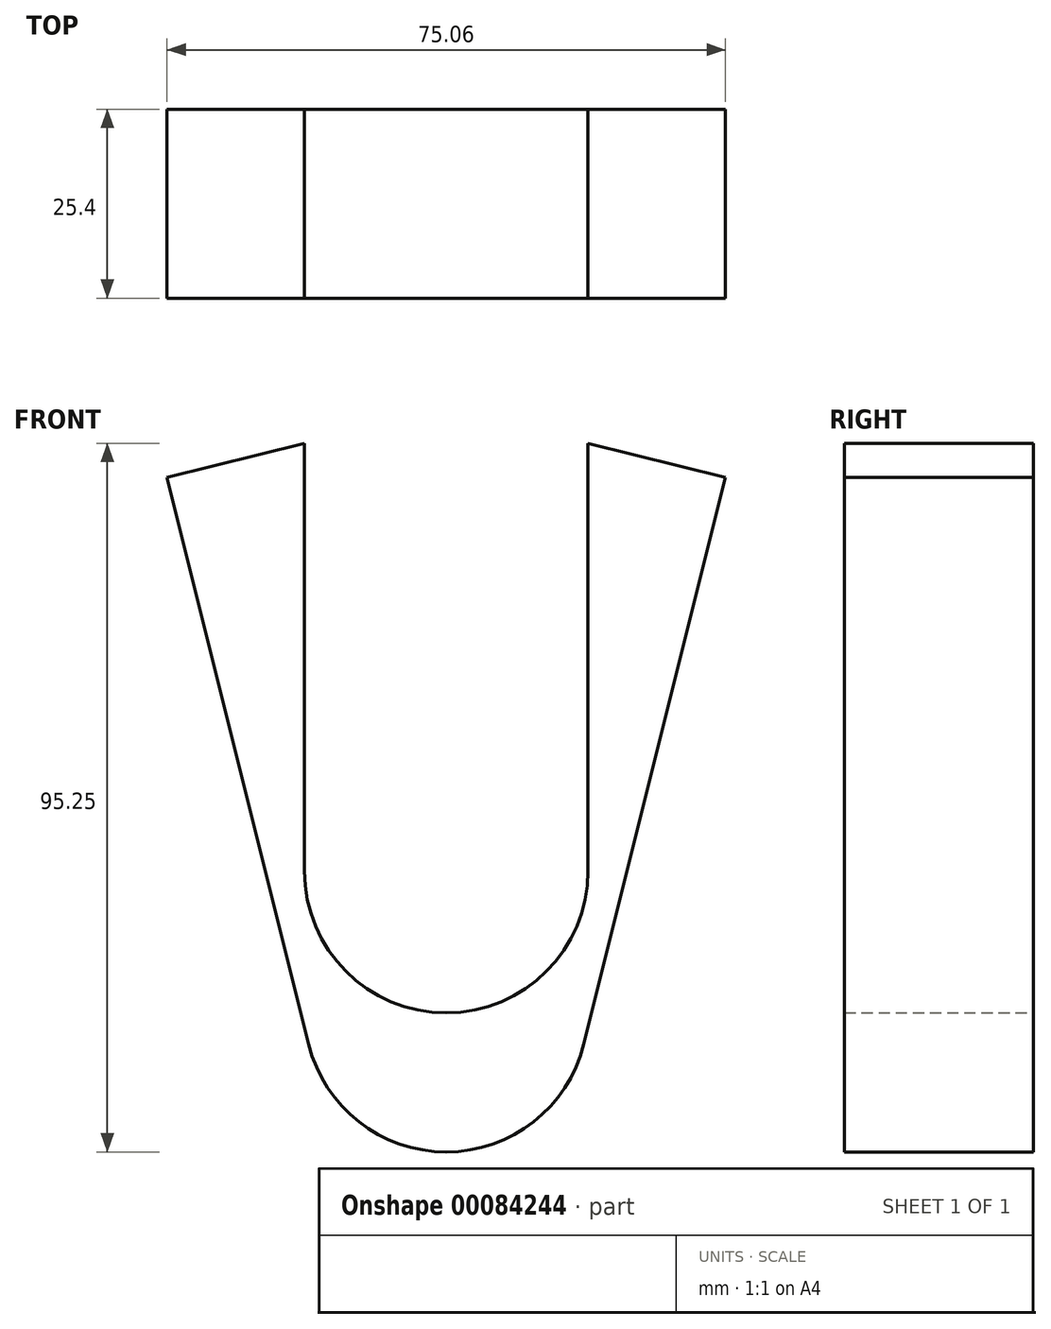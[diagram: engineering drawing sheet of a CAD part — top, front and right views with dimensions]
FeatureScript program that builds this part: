
annotation { "Feature Type Name" : "Feature", "Feature Type Description" : "" }
export const myFeature = defineFeature(function(context is Context, id is Id, definition is map)
    precondition{}
    {
        {
            var Q0;
            Q0=qCreatedBy(makeId("Front.planeOp"),FACE);
            var sketch = newSketch(context, id + "F0", { "sketchPlane" : qUnion([Q0])});
            skLineSegment(sketch, "E0", {"start": v(0, 0) * mm, "end": v(19.05, 0) * mm, "construction": true});
            skLineSegment(sketch, "E1", {"start": v(0, 0) * mm, "end": v(0, -76.2) * mm, "construction": true});
            skLineSegment(sketch, "E2", {"start": v(19.05, 0) * mm, "end": v(-19.05, 0) * mm, "construction": true});
            skLineSegment(sketch, "E3", {"start": v(19.05, 0) * mm, "end": v(0, -76.2) * mm});
            skLineSegment(sketch, "E4", {"start": v(-19.05, 0) * mm, "end": v(0, -76.2) * mm});
            skLineSegment(sketch, "E5", {"start": v(19.05, 0) * mm, "end": v(37.53, -4.62) * mm});
            skLineSegment(sketch, "E6", {"start": v(0, -76.2) * mm, "end": v(18.48, -80.82) * mm});
            skLineSegment(sketch, "E7", {"start": v(37.53, -4.62) * mm, "end": v(18.48, -80.82) * mm});
            skLineSegment(sketch, "E8.MirrorCS", {"start": v(-19.05, 0) * mm, "end": v(-37.53, -4.62) * mm});
            skLineSegment(sketch, "E9.MirrorCS", {"start": v(-37.53, -4.62) * mm, "end": v(-18.48, -80.82) * mm});
            skLineSegment(sketch, "E10.MirrorCS", {"start": v(0, -76.2) * mm, "end": v(-18.48, -80.82) * mm});
            skArc(sketch, "E11", {"start": v(-18.48, -80.82) * mm, "mid": v(0, -95.25) * mm, "end": v(18.48, -80.82) * mm});
            skSolve(sketch);
        }
        {
            var Q0;
            Q0 = qSketchRegion(id + "F0", true);
            extrude(context, id + "F1", {"entities" : qUnion([Q0]), "endBound" : BoundingType.SYMMETRIC, "depth" : 25.4 * mm});
        }
        {
            var Q0;
            Q0=qCreatedBy(makeId("Front.planeOp"),FACE);
            var sketch = newSketch(context, id + "F2", { "sketchPlane" : qUnion([Q0])});
            skLineSegment(sketch, "E12", {"start": v(0, 0) * mm, "end": v(19.05, 0) * mm, "construction": true});
            skLineSegment(sketch, "E13", {"start": v(0, 0) * mm, "end": v(0, -76.55) * mm, "construction": true});
            skLineSegment(sketch, "E14", {"start": v(-19.05, -57.5) * mm, "end": v(-19.05, 0) * mm});
            skLineSegment(sketch, "E15", {"start": v(19.05, -57.5) * mm, "end": v(19.05, 0) * mm});
            skLineSegment(sketch, "E16", {"start": v(-19.05, 0) * mm, "end": v(19.05, 0) * mm});
            skArc(sketch, "E17", {"start": v(-19.05, -57.5) * mm, "mid": v(0, -76.56) * mm, "end": v(19.05, -57.5) * mm});
            skSolve(sketch);
        }
        {
            var Q0;
            Q0 = qSketchRegion(id + "F2", true);
            extrude(context, id + "F3", {"entities" : qUnion([Q0]), "operationType" : NewBodyOperationType.REMOVE, "endBound" : BoundingType.SYMMETRIC, "depth" : 25.4 * mm});
        }
    });
